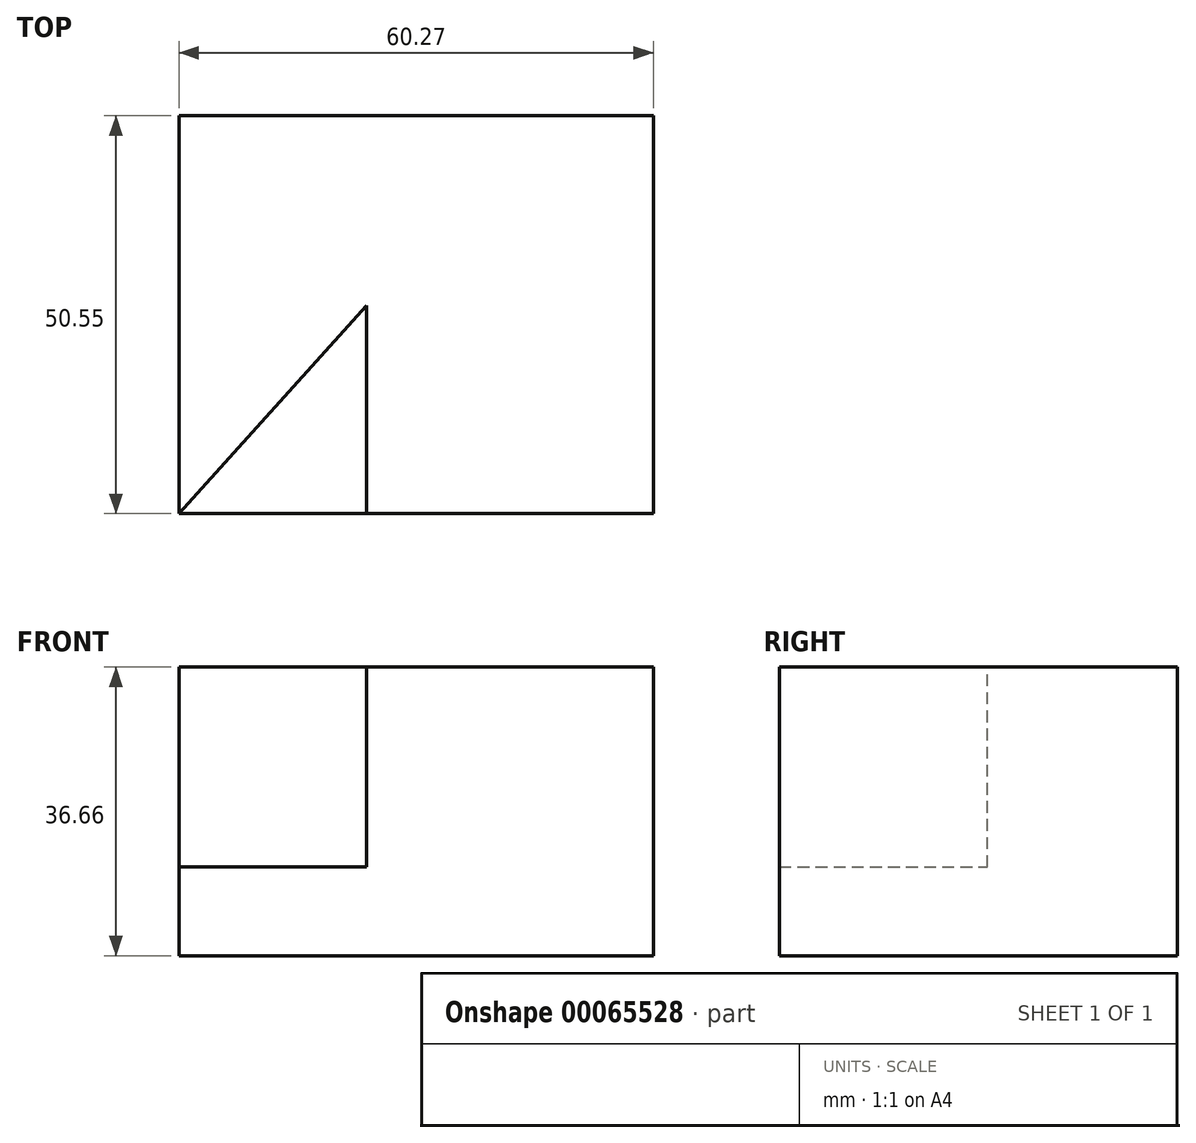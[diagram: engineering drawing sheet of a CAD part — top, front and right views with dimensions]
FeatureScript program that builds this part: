
annotation { "Feature Type Name" : "Feature", "Feature Type Description" : "" }
export const myFeature = defineFeature(function(context is Context, id is Id, definition is map)
    precondition{}
    {
        {
            var Q0;
            Q0=qCreatedBy(makeId("Top.planeOp"),FACE);
            var sketch = newSketch(context, id + "F0", { "sketchPlane" : qUnion([Q0])});
            skLineSegment(sketch, "E0.bottom", {"start": v(-23.84, 24.13) * mm, "end": v(36.43, 24.13) * mm});
            skLineSegment(sketch, "E0.top", {"start": v(-23.84, -26.42) * mm, "end": v(36.43, -26.42) * mm});
            skLineSegment(sketch, "E0.left", {"start": v(-23.84, 24.13) * mm, "end": v(-23.84, -26.42) * mm});
            skLineSegment(sketch, "E0.right", {"start": v(36.43, 24.13) * mm, "end": v(36.43, -26.42) * mm});
            skSolve(sketch);
        }
        {
            var Q0;
            Q0=makeQuery(id+"F0.imprint","IMPRINT",FACE,{"disambiguationData":[TD([[makeQuery(id+"F0.imprint","IMPRINT",EDGE,{"derivedFrom":sQuery(id+"F0.wireOp",EDGE,"E0.bottom")}),-1.0]])]});
            extrude(context, id + "F1", {"entities" : qUnion([Q0]), "depth" : 36.66 * mm});
        }
        {
            var Q0;
            Q0=makeQuery(id+"F1.opExtrude","CAP_FACE",FACE,{"disambiguationData":[OSD([sQuery(id+"F0.wireOp",EDGE,"E0.bottom"),sQuery(id+"F0.wireOp",EDGE,"E0.top"),sQuery(id+"F0.wireOp",EDGE,"E0.left"),sQuery(id+"F0.wireOp",EDGE,"E0.right")])],"isStart":false});
            var sketch = newSketch(context, id + "F2", { "sketchPlane" : qUnion([Q0])});
            skLineSegment(sketch, "E1", {"start": v(-23.84, -26.42) * mm, "end": v(0, 0) * mm});
            skLineSegment(sketch, "E2", {"start": v(0, 0) * mm, "end": v(0, -26.42) * mm});
            skLineSegment(sketch, "E3", {"start": v(0, -26.42) * mm, "end": v(-23.84, -26.42) * mm});
            skSolve(sketch);
        }
        {
            var Q0;
            Q0=makeQuery(id+"F2.imprint","IMPRINT",FACE,{"disambiguationData":[TD([[makeQuery(id+"F2.imprint","IMPRINT",EDGE,{"derivedFrom":sQuery(id+"F2.wireOp",EDGE,"E1")}),-1.0]])]});
            extrude(context, id + "F3", {"entities" : qUnion([Q0]), "operationType" : NewBodyOperationType.REMOVE, "oppositeDirection" : true, "depth" : 25.4 * mm});
        }
    });
